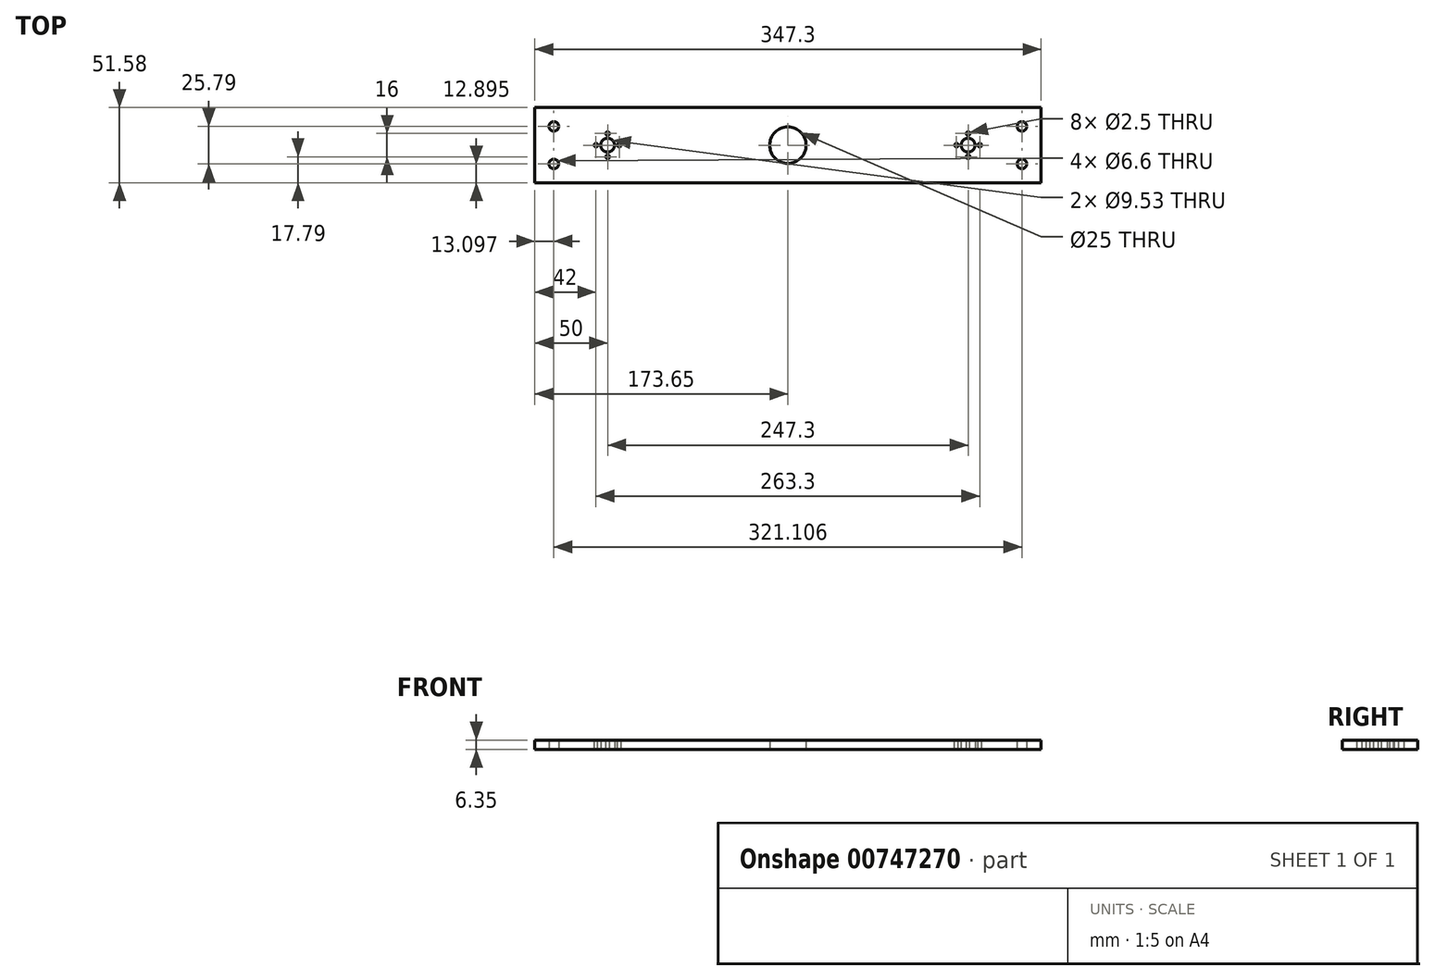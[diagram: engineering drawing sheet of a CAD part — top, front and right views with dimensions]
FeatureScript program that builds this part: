
annotation { "Feature Type Name" : "Feature", "Feature Type Description" : "" }
export const myFeature = defineFeature(function(context is Context, id is Id, definition is map)
    precondition{}
    {
        {
            var Q0;
            Q0=qCreatedBy(makeId("Top.planeOp"),FACE);
            var sketch = newSketch(context, id + "F0", { "sketchPlane" : qUnion([Q0])});
            skLineSegment(sketch, "E0.bottom", {"start": v(173.65, 25.79) * mm, "end": v(-173.65, 25.8) * mm});
            skLineSegment(sketch, "E0.top", {"start": v(173.65, -25.8) * mm, "end": v(-173.65, -25.79) * mm});
            skLineSegment(sketch, "E0.left", {"start": v(173.65, 25.79) * mm, "end": v(173.65, -25.79) * mm});
            skLineSegment(sketch, "E0.right", {"start": v(-173.65, 25.8) * mm, "end": v(-173.65, -25.8) * mm});
            skPoint(sketch, "E0.middle", {"position": v(0, 0) * mm});
            skLineSegment(sketch, "E1", {"start": v(-173.65, 0) * mm, "end": v(173.65, 0) * mm, "construction": true});
            skPoint(sketch, "E2", {"position": v(-123.65, 0) * mm});
            skPoint(sketch, "E3", {"position": v(123.65, 0) * mm});
            skCircle(sketch, "E4", {"center": v(-123.65, 0) * mm, "radius": 4.76 * mm});
            skCircle(sketch, "E5", {"center": v(0, 0) * mm, "radius": 12.5 * mm});
            skCircle(sketch, "E6", {"center": v(123.65, 0) * mm, "radius": 4.76 * mm});
            skSolve(sketch);
        }
        {
            var Q0;
            Q0=qSketchRegion(id+"F0",true);
            extrude(context, id + "F1", {"entities" : qUnion([Q0]), "depth" : 6.35 * mm, "offsetDistance" : 25 * mm});
        }
        {
            var Q0;
            Q0=makeQuery(id+"F1.opExtrude","CAP_FACE",FACE,{"disambiguationData":[OSD([sQuery(id+"F0.wireOp",EDGE,"E0.bottom"),sQuery(id+"F0.wireOp",EDGE,"E0.top"),sQuery(id+"F0.wireOp",EDGE,"E0.left"),sQuery(id+"F0.wireOp",EDGE,"E0.right"),sQuery(id+"F0.wireOp",EDGE,"E4"),sQuery(id+"F0.wireOp",EDGE,"E5"),sQuery(id+"F0.wireOp",EDGE,"E6")])],"isStart":true});
            var sketch = newSketch(context, id + "F2", { "sketchPlane" : qUnion([Q0])});
            skLineSegment(sketch, "E7", {"start": v(-173.65, 0) * mm, "end": v(173.65, 0) * mm, "construction": true});
            skLineSegment(sketch, "E8", {"start": v(-173.65, 0) * mm, "end": v(-173.65, 25.8) * mm, "construction": true});
            skLineSegment(sketch, "E9", {"start": v(-173.65, 0) * mm, "end": v(-173.65, -25.8) * mm, "construction": true});
            skLineSegment(sketch, "E10", {"start": v(-173.65, 12.9) * mm, "end": v(-160.55, 12.9) * mm, "construction": true});
            skLineSegment(sketch, "E11", {"start": v(-173.65, -12.9) * mm, "end": v(-160.55, -12.9) * mm, "construction": true});
            skLineSegment(sketch, "E12", {"start": v(173.65, 0) * mm, "end": v(173.65, 25.79) * mm, "construction": true});
            skLineSegment(sketch, "E13", {"start": v(173.65, 0) * mm, "end": v(173.65, -25.79) * mm, "construction": true});
            skLineSegment(sketch, "E14", {"start": v(173.65, -12.9) * mm, "end": v(160.55, -12.9) * mm, "construction": true});
            skLineSegment(sketch, "E15", {"start": v(173.65, 12.9) * mm, "end": v(160.55, 12.9) * mm, "construction": true});
            skSolve(sketch);
        }
        {
            var Q0;
            Q0=sQuery(id+"F2.wireOp",VERTEX,"E10.end");
            var Q1;
            Q1=sQuery(id+"F2.wireOp",VERTEX,"E11.end");
            var Q2;
            Q2=sQuery(id+"F2.wireOp",VERTEX,"E15.end");
            var Q3;
            Q3=sQuery(id+"F2.wireOp",VERTEX,"E14.end");
            var Q4;
            Q4=makeQuery(id+"F1.opExtrude","SWEPT_BODY",BODY,{"disambiguationData":[OSD([sQuery(id+"F0.wireOp",EDGE,"E0.bottom"),sQuery(id+"F0.wireOp",EDGE,"E0.top"),sQuery(id+"F0.wireOp",EDGE,"E0.left"),sQuery(id+"F0.wireOp",EDGE,"E0.right"),sQuery(id+"F0.wireOp",EDGE,"E4"),sQuery(id+"F0.wireOp",EDGE,"E5"),sQuery(id+"F0.wireOp",EDGE,"E6")])]});
            hole(context, id + "F3", {"style" : HoleStyle.SIMPLE, "endStyle" : HoleEndStyle.THROUGH, "standardTappedOrClearance" : lookupTablePath({ "standard" : "ISO", "fit" : "Normal", "size" : "M6", "type" : "Clearance" }), "standardBlindInLast" : lookupTablePath({ "fit" : "Standard", "standard" : "ISO", "size" : "M6", "type" : "Clearance" }), "holeDiameter" : 6.6 * mm, "majorDiameter" : 5 * mm, "isTappedThrough" : true, "tappedDepth" : 12 * mm, "tapClearance" : 3, "locations" : qUnion([Q0, Q1, Q2, Q3]), "scope" : qUnion([Q4])});
        }
        {
            var Q0;
            Q0=makeQuery(id+"F1.opExtrude","CAP_FACE",FACE,{"disambiguationData":[OSD([sQuery(id+"F0.wireOp",EDGE,"E0.bottom"),sQuery(id+"F0.wireOp",EDGE,"E0.top"),sQuery(id+"F0.wireOp",EDGE,"E0.left"),sQuery(id+"F0.wireOp",EDGE,"E0.right"),sQuery(id+"F0.wireOp",EDGE,"E4"),sQuery(id+"F0.wireOp",EDGE,"E5"),sQuery(id+"F0.wireOp",EDGE,"E6")])],"isStart":false});
            var sketch = newSketch(context, id + "F4", { "sketchPlane" : qUnion([Q0])});
            skLineSegment(sketch, "E16", {"start": v(-173.65, 0) * mm, "end": v(173.65, 0) * mm, "construction": true});
            skCircle(sketch, "E17", {"center": v(-123.65, 0) * mm, "radius": 8 * mm, "construction": true});
            skCircle(sketch, "E18", {"center": v(123.65, 0) * mm, "radius": 8 * mm, "construction": true});
            skLineSegment(sketch, "E19", {"start": v(-123.65, 0) * mm, "end": v(-123.65, 8) * mm});
            skLineSegment(sketch, "E20", {"start": v(-123.65, 8) * mm, "end": v(-123.65, -8) * mm});
            skLineSegment(sketch, "E21", {"start": v(123.65, 0) * mm, "end": v(123.65, 8) * mm, "construction": true});
            skLineSegment(sketch, "E22", {"start": v(123.65, 8) * mm, "end": v(123.65, -8) * mm, "construction": true});
            skPoint(sketch, "E23", {"position": v(-131.65, 0) * mm});
            skPoint(sketch, "E24", {"position": v(-115.65, 0) * mm});
            skPoint(sketch, "E25", {"position": v(131.65, 0) * mm});
            skPoint(sketch, "E26", {"position": v(115.65, 0) * mm});
            skSolve(sketch);
        }
        {
            var Q0;
            Q0=sQuery(id+"F4.wireOp",VERTEX,"E20.start");
            var Q1;
            Q1=sQuery(id+"F4.wireOp",VERTEX,"E24");
            var Q2;
            Q2=sQuery(id+"F4.wireOp",VERTEX,"E20.end");
            var Q3;
            Q3=sQuery(id+"F4.wireOp",VERTEX,"E23");
            var Q4;
            Q4=sQuery(id+"F4.wireOp",VERTEX,"E22.start");
            var Q5;
            Q5=sQuery(id+"F4.wireOp",VERTEX,"E25");
            var Q6;
            Q6=sQuery(id+"F4.wireOp",VERTEX,"E22.end");
            var Q7;
            Q7=sQuery(id+"F4.wireOp",VERTEX,"E26");
            var Q8;
            Q8=makeQuery(id+"F1.opExtrude","SWEPT_BODY",BODY,{"disambiguationData":[OSD([sQuery(id+"F0.wireOp",EDGE,"E0.bottom"),sQuery(id+"F0.wireOp",EDGE,"E0.top"),sQuery(id+"F0.wireOp",EDGE,"E0.left"),sQuery(id+"F0.wireOp",EDGE,"E0.right"),sQuery(id+"F0.wireOp",EDGE,"E4"),sQuery(id+"F0.wireOp",EDGE,"E5"),sQuery(id+"F0.wireOp",EDGE,"E6")])]});
            hole(context, id + "F5", {"style" : HoleStyle.SIMPLE, "endStyle" : HoleEndStyle.THROUGH, "standardTappedOrClearance" : lookupTablePath({ "standard" : "ISO", "engagement" : "75%", "pitch" : "0.5 mm", "size" : "M3", "type" : "Tapped" }), "standardBlindInLast" : lookupTablePath({ "standard" : "ISO", "engagement" : "75%", "pitch" : "0.5 mm", "size" : "M3", "type" : "Tapped" }), "holeDiameter" : 2.5 * mm, "majorDiameter" : 3 * mm, "showTappedDepth" : true, "isTappedThrough" : true, "tappedDepth" : 12 * mm, "tapClearance" : 3, "locations" : qUnion([Q0, Q1, Q2, Q3, Q4, Q5, Q6, Q7]), "scope" : qUnion([Q8])});
        }
    });
